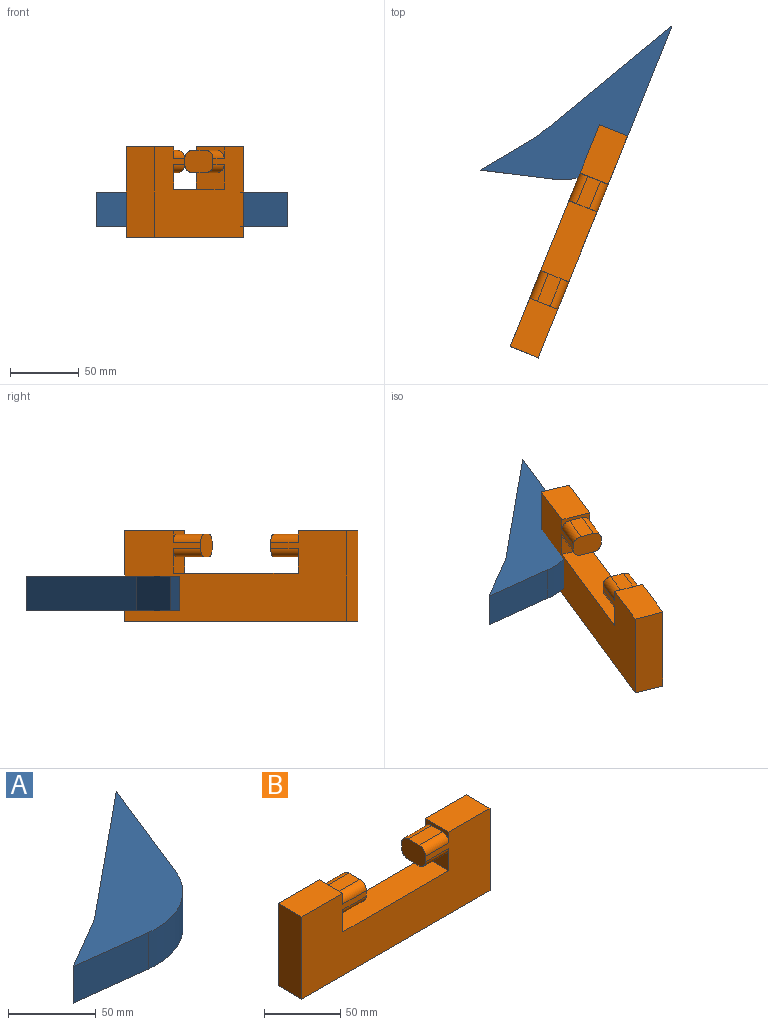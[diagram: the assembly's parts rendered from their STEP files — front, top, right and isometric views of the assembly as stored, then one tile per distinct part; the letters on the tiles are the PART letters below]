
ASSEMBLY  parts=2 mates=1
PART A: 7 faces, bbox 139.5x111.8x25.4 mm
  f0: cylinder r=50.8mm len=53.32mm, axis (0,0,-1), area 1690.5mm2, adj f1,f4,f5,f6
  f1: plane 80.01x32.23mm, normal (0.93,-0.37,0), area 2190.9mm2, adj f0,f2,f5,f6
  f2: plane 98.17x80.57mm, normal (-0.63,0.77,0), area 3225.8mm2, adj f1,f3,f5,f6
  f3: plane 41.33x25.4mm, normal (-0.51,0.86,0), area 1217mm2, adj f2,f4,f5,f6
  f4: plane 53.95x25.4mm, normal (-0.12,-0.99,0), area 1380.7mm2, adj f0,f3,f5,f6
  f5: plane 139.5x111.83mm, normal (0,0,1), area 4885.1mm2, adj f0,f1,f2,f3,f4
  f6: plane 139.5x111.83mm, normal (0,0,-1), area 4885.1mm2, adj f0,f1,f2,f3,f4
PART B: 26 faces, bbox 174x22x65.8 mm
  f0: plane 21.59x10mm, normal (0,0,1), area 215.9mm2, adj f4,f8,f9,f10
  f1: plane 21.59x10mm, normal (0,0,1), area 215.9mm2, adj f5,f13,f14,f15
  f2: plane 21.59x10mm, normal (0,0,-1), area 215.9mm2, adj f6,f15,f16,f17
  f3: plane 21.59x10mm, normal (0,0,-1), area 215.9mm2, adj f7,f8,f19,f20
  f4: cylinder r=6mm len=21.59mm, axis (-1,0,0), area 203.5mm2, adj f0,f8,f10,f22
  f5: cylinder r=6mm len=21.59mm, axis (-1,0,0), area 203.5mm2, adj f1,f13,f15,f22
  f6: cylinder r=6mm len=21.59mm, axis (1,0,0), area 203.5mm2, adj f2,f15,f17,f22
  f7: cylinder r=6mm len=21.59mm, axis (1,0,0), area 203.5mm2, adj f3,f8,f19,f22
  f8: plane 22x16.45mm, normal (-1,0,0), area 330.9mm2, adj f0,f3,f4,f7,f9,f20,f22,f24
  f9: cylinder r=6mm len=21.59mm, axis (1,0,0), area 203.5mm2, adj f0,f8,f10,f24
  f10: plane 22x8.58mm, normal (-1,0,0), area 72.3mm2, adj f0,f4,f9,f11,f22,f24
  f11: plane 38x22mm, normal (0,0,1), area 836mm2, adj f10,f12,f22,f24
  f12: plane 65.8x22mm, normal (1,0,0), area 1447.6mm2, adj f11,f22,f23,f24
  f13: plane 22x8.58mm, normal (1,0,0), area 72.3mm2, adj f1,f5,f14,f21,f22,f24
  f14: cylinder r=6mm len=21.59mm, axis (1,0,0), area 203.5mm2, adj f1,f13,f15,f24
  f15: plane 22x16.45mm, normal (1,0,0), area 330.9mm2, adj f1,f2,f5,f6,f14,f16,f22,f24
  f16: cylinder r=6mm len=21.59mm, axis (-1,0,0), area 203.5mm2, adj f2,f15,f17,f24
  f17: plane 22x17.77mm, normal (1,0,0), area 274.4mm2, adj f2,f6,f16,f18,f22,f24
  f18: plane 98x22mm, normal (0,0,1), area 2156mm2, adj f17,f19,f22,f24
  f19: plane 22x17.77mm, normal (-1,0,0), area 274.4mm2, adj f3,f7,f18,f20,f22,f24
  f20: cylinder r=6mm len=21.59mm, axis (-1,0,0), area 203.5mm2, adj f3,f8,f19,f24
  f21: plane 38x22mm, normal (0,0,1), area 836mm2, adj f13,f22,f24,f25
  f22: plane 174x65.8mm, normal (0,-1,0), area 8622.8mm2, adj f4,f5,f6,f7,f8,f10,f11,f12
  f23: plane 174x22mm, normal (0,0,-1), area 3828mm2, adj f12,f22,f24,f25
  f24: plane 174x65.8mm, normal (0,1,0), area 8622.8mm2, adj f8,f9,f10,f11,f12,f13,f14,f15
  f25: plane 65.8x22mm, normal (-1,0,0), area 1447.6mm2, adj f21,f22,f23,f24
PLACE A t=(-29.01,-25.21,-13.01)mm
PLACE B rot(axis=(0,0,1),68.1deg) t=(-15.99,-97.12,-20.51)mm
MATE parallel B.f22 <-> A.f1  axis (0.93,-0.37,0) through (36.93,-24.64,12.39)mm
